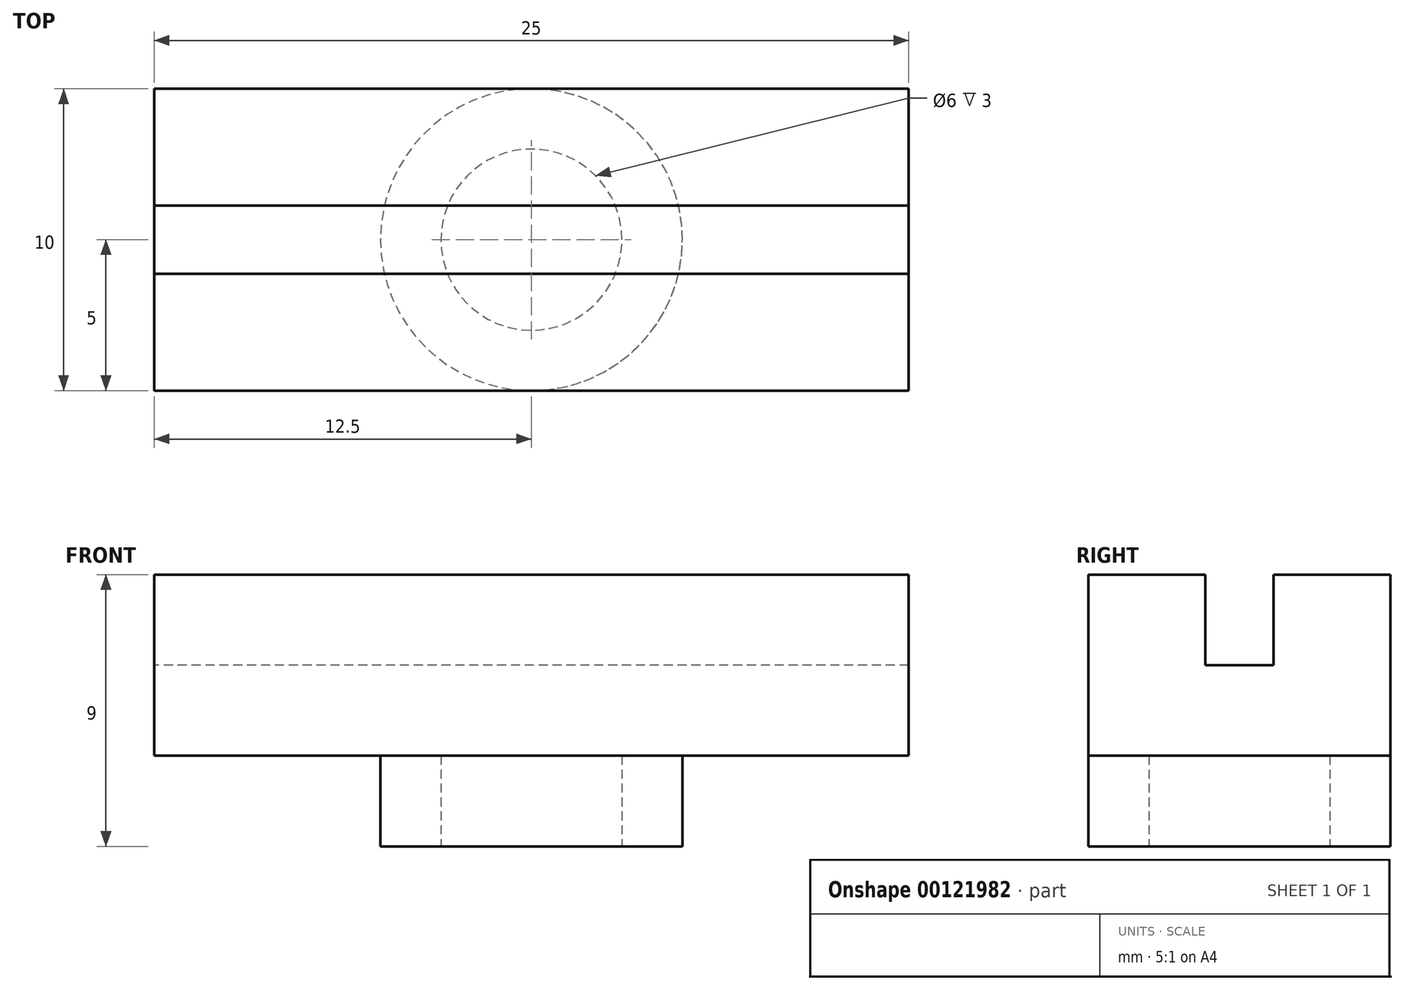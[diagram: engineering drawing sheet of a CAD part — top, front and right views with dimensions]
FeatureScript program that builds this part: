
annotation { "Feature Type Name" : "Feature", "Feature Type Description" : "" }
export const myFeature = defineFeature(function(context is Context, id is Id, definition is map)
    precondition{}
    {
        {
            var Q0;
            Q0=qCreatedBy(makeId("Top.planeOp"),FACE);
            var sketch = newSketch(context, id + "F0", { "sketchPlane" : qUnion([Q0])});
            skCircle(sketch, "E0", {"center": v(0, 0) * mm, "radius": 5 * mm});
            skSolve(sketch);
        }
        {
            var Q0;
            Q0 = qSketchRegion(id + "F0", true);
            extrude(context, id + "F1", {"entities" : qUnion([Q0]), "depth" : 3 * mm});
        }
        {
            var Q0;
            Q0=qCreatedBy(makeId("Top.planeOp"),FACE);
            var sketch = newSketch(context, id + "F2", { "sketchPlane" : qUnion([Q0])});
            skCircle(sketch, "E1", {"center": v(0, 0) * mm, "radius": 3 * mm});
            skSolve(sketch);
        }
        {
            var Q0;
            Q0 = qSketchRegion(id + "F2", true);
            extrude(context, id + "F3", {"entities" : qUnion([Q0]), "operationType" : NewBodyOperationType.REMOVE, "depth" : 3 * mm});
        }
        {
            var Q0;
            Q0=makeQuery(id+"F1.opExtrude","CAP_FACE",FACE,{"disambiguationData":[OSD([sQuery(id+"F0.wireOp",EDGE,"E0")])],"isStart":false});
            var sketch = newSketch(context, id + "F4", { "sketchPlane" : qUnion([Q0])});
            skLineSegment(sketch, "E2.bottom", {"start": v(12.5, -5) * mm, "end": v(-12.5, -5) * mm});
            skLineSegment(sketch, "E2.top", {"start": v(12.5, 5) * mm, "end": v(-12.5, 5) * mm});
            skLineSegment(sketch, "E2.left", {"start": v(12.5, -5) * mm, "end": v(12.5, 5) * mm});
            skLineSegment(sketch, "E2.right", {"start": v(-12.5, -5) * mm, "end": v(-12.5, 5) * mm});
            skPoint(sketch, "E2.middle", {"position": v(0, 0) * mm});
            skSolve(sketch);
        }
        {
            var Q0;
            Q0 = qSketchRegion(id + "F4", true);
            extrude(context, id + "F5", {"entities" : qUnion([Q0]), "operationType" : NewBodyOperationType.ADD, "depth" : 6 * mm});
        }
        {
            var Q0;
            Q0=makeQuery(id+"F5.opExtrude","CAP_FACE",FACE,{"disambiguationData":[OSD([sQuery(id+"F4.wireOp",EDGE,"E2.bottom"),sQuery(id+"F4.wireOp",EDGE,"E2.top"),sQuery(id+"F4.wireOp",EDGE,"E2.left"),sQuery(id+"F4.wireOp",EDGE,"E2.right")])],"isStart":false});
            var sketch = newSketch(context, id + "F6", { "sketchPlane" : qUnion([Q0])});
            skLineSegment(sketch, "E3.bottom", {"start": v(12.5, -1.13) * mm, "end": v(-12.5, -1.13) * mm});
            skLineSegment(sketch, "E3.top", {"start": v(12.5, 1.12) * mm, "end": v(-12.5, 1.12) * mm});
            skLineSegment(sketch, "E3.left", {"start": v(12.5, -1.13) * mm, "end": v(12.5, 1.12) * mm});
            skLineSegment(sketch, "E3.right", {"start": v(-12.5, -1.13) * mm, "end": v(-12.5, 1.12) * mm});
            skPoint(sketch, "E3.middle", {"position": v(0, 0) * mm});
            skSolve(sketch);
        }
        {
            var Q0;
            Q0 = qSketchRegion(id + "F6", true);
            extrude(context, id + "F7", {"entities" : qUnion([Q0]), "operationType" : NewBodyOperationType.REMOVE, "oppositeDirection" : true, "depth" : 3 * mm});
        }
    });
